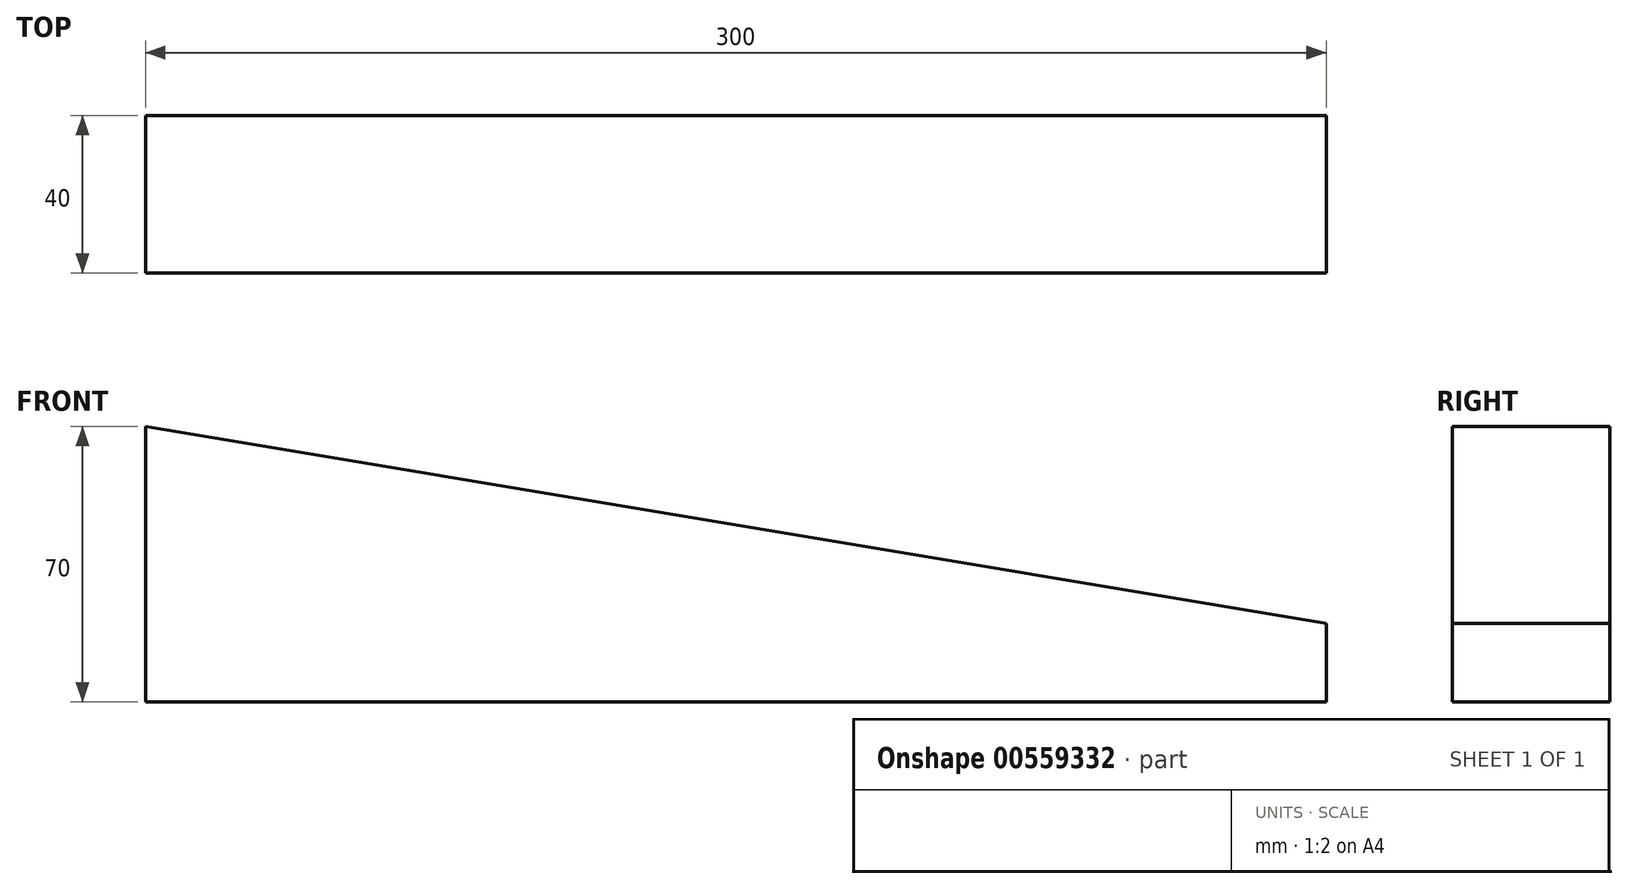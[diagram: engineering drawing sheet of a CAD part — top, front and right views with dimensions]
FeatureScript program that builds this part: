
annotation { "Feature Type Name" : "Feature", "Feature Type Description" : "" }
export const myFeature = defineFeature(function(context is Context, id is Id, definition is map)
    precondition{}
    {
        {
            var Q0;
            Q0=qCreatedBy(makeId("Front.planeOp"),FACE);
            var sketch = newSketch(context, id + "F0", { "sketchPlane" : qUnion([Q0])});
            skLineSegment(sketch, "E0", {"start": v(0, 0) * mm, "end": v(0, 70) * mm});
            skLineSegment(sketch, "E1", {"start": v(0, 0) * mm, "end": v(300, 0) * mm});
            skLineSegment(sketch, "E2", {"start": v(300, 0) * mm, "end": v(300, 20) * mm});
            skLineSegment(sketch, "E3", {"start": v(300, 20) * mm, "end": v(0, 70) * mm});
            skSolve(sketch);
        }
        {
            var Q0;
            Q0=makeQuery(id+"F0.imprint","IMPRINT",FACE,{"disambiguationData":[TD([[makeQuery(id+"F0.imprint","IMPRINT",EDGE,{"derivedFrom":sQuery(id+"F0.wireOp",EDGE,"E0")}),-1.0]])]});
            extrude(context, id + "F1", {"entities" : qUnion([Q0]), "depth" : 40 * mm, "offsetDistance" : 25 * mm});
        }
        {
            var Q0;
            Q0=makeQuery(id+"F1.opExtrude","SWEPT_FACE",FACE,{"disambiguationData":[OSD([sQuery(id+"F0.wireOp",EDGE,"E0")])]});
            var sketch = newSketch(context, id + "F2", { "sketchPlane" : qUnion([Q0])});
            skFitSpline(sketch, "E4", {"points": [v(0, 35) * mm, v(20, 70) * mm, v(40, 35) * mm, v(20, 0) * mm, v(0, 35) * mm]});
            skSolve(sketch);
        }
        {
            var Q0;
            Q0=makeQuery(id+"F1.opExtrude","SWEPT_FACE",FACE,{"disambiguationData":[OSD([sQuery(id+"F0.wireOp",EDGE,"E2")])]});
            var sketch = newSketch(context, id + "F3", { "sketchPlane" : qUnion([Q0])});
            skFitSpline(sketch, "E5", {"points": [v(-40, 10) * mm, v(-20, 20) * mm, v(0, 10) * mm, v(-20, 0) * mm, v(-40, 10) * mm]});
            skSolve(sketch);
        }
        {
            var Q0;
            Q0=sQuery(id+"F2.wireOp",EDGE,"E4");
            var Q1;
            Q1=sQuery(id+"F3.wireOp",EDGE,"E5");
            loft(context, id + "F4", {"bodyType" : ToolBodyType.SURFACE, "wireProfilesArray" : [{ "wireProfileEntities" : qUnion([Q0]) }, { "wireProfileEntities" : qUnion([Q1]) }]});
        }
    });
